# Revit family: Поли-Групп_КлапанОбратныйEAZ-RP_DN100-700
name_source: partatom
category: Арматура трубопроводов
units: mm (PartAtom-declared; Revit-internal decimal feet)

## family parameters
Всегда вертикально = Да
На основе рабочей плоскости = Нет
Общий = Нет
При загрузке вырезать с полостями = Нет
Размер круглого соединителя = Использовать диаметр
Тип детали = Нормальный

## types (19) — shared parameters
ADSK_URL страницы изделия = https://www.polycorr.ru
ADSK_Версия Revit = 2019
ADSK_Единица измерения = шт.
ADSK_Завод-изготовитель = ООО ПК Поли-Групп
ADSK_Количество = 1
ADSK_Материал = Высокопрочный чугун GGG-40
ADSK_Материал наименование = Высокопрочный чугун с шаровидным графитом (GGG-40)
Класс герметичности = А по ГОСТ Р 9544-2015
Материал диска = Высокотемпературная углеродистая сталь
Материал диска/шара/створки = Бронза CuSn10
Материал уплотнителя = NBR
Назначение = Для предотвращения обратного потока среды на горизонтальных трубопроводах
Покрытие = Высококачественное эпоксидное покрытие толщиной 300 мкм
Рабочая среда = Питьевая вода, техническая вода, канализационные стоки, морская вода
Разработчик = https://3dbim.pro
Срок службы = 50 лет
ТВ = КлапанОбратныйEAZ-RP_DN100-700_Поли-Групп
Температура рабочей среды = 0 до +70°С
Тип привода = Без привода
Тип присоединения = Фланцевое
zero-valued in all types: D1

## per-type parameters (varying)
| type | ADSK_Диаметр условный | ADSK_Марка | ADSK_Масса | ADSK_Масса_Текст | ADSK_Наименование | ADSK_Наименование краткое | D | D2 | DN | H1 | H2 | L | PN | b | d3 | d4 | d5 | f | r | Габаритные размеры |
| 200-10 | 200 мм | EAZ-DCh-2 DN200 PN10 | 117 | 117 | Клапан обратный EAZ RP с рычагом и противовесом для горизонтальной установки фланцевый DN200 PN10 | Клапан обратный EAZ RP DN200 PN10 | 340 мм | 266 мм | 200 мм | 40 мм | 250 мм | 500 мм | 10.0 бары | 20 мм | 240 мм | 220 мм | 200 мм | 3 мм | 156 мм | 295х340х460 |
| 250-10 | 250 мм | EAZ-DCh-2 DN250 PN10 | 170 | 170 | Клапан обратный EAZ RP с рычагом и противовесом для горизонтальной установки фланцевый DN250 PN10 | Клапан обратный EAZ RP DN250 PN10 | 405 мм | 319 мм | 250 мм | 49 мм | 284 мм | 600 мм | 10.0 бары | 22 мм | 300 мм | 275 мм | 250 мм | 3 мм | 195 мм | 355х405х536 |
| 300-10 | 300 мм | EAZ-DCh-2 DN300 PN10 | 263 | 263 | Клапан обратный EAZ RP с рычагом и противовесом для горизонтальной установки фланцевый DN300 PN10 | Клапан обратный EAZ RP DN300 PN10 | 445 мм | 370 мм | 300 мм | 58 мм | 318 мм | 700 мм | 10.0 бары | 25 мм | 360 мм | 330 мм | 300 мм | 4 мм | 234 мм | 400х445х599 |
| 350-10 | 350 мм | EAZ-DCh-2 DN350 PN10 | 320 | 320 | Клапан обратный EAZ RP с рычагом и противовесом для горизонтальной установки фланцевый DN350 PN10 | Клапан обратный EAZ RP DN350 PN10 | 520 мм | 429 мм | 350 мм | 69 мм | 354 мм | 800 мм | 10.0 бары | 25 мм | 420 мм | 385 мм | 350 мм | 4 мм | 273 мм | 470х520х683 |
| 400-10 | 400 мм | EAZ-DCh-2 DN400 PN10 | 485 | 485 | Клапан обратный EAZ RP с рычагом и противовесом для горизонтальной установки фланцевый DN400 PN10 | Клапан обратный EAZ RP DN400 PN10 | 656 мм | 480 мм | 400 мм | 79 мм | 390 мм | 900 мм | 10.0 бары | 25 мм | 480 мм | 440 мм | 400 мм | 4 мм | 312 мм | 515х656х797 |
| 500-10 | 500 мм | EAZ-DCh-2 DN500 PN10 | 620 | 620 | Клапан обратный EAZ RP с рычагом и противовесом для горизонтальной установки фланцевый DN500 PN10 | Клапан обратный EAZ RP DN500 PN10 | 670 мм | 582 мм | 500 мм | 62 мм | 497 мм | 1100 мм | 10.0 бары | 27 мм | 600 мм | 550 мм | 500 мм | 4 мм | 390 мм | 620х670х894 |
| 600-10 | 600 мм | EAZ-DCh-2 DN600 PN10 | 910 | 910 | Клапан обратный EAZ RP с рычагом и противовесом для горизонтальной установки фланцевый DN600 PN10 | Клапан обратный EAZ RP DN600 PN10 | 780 мм | 682 мм | 600 мм | 62 мм | 550 мм | 1300 мм | 10.0 бары | 30 мм | 720 мм | 660 мм | 600 мм | 5 мм | 468 мм | 725х780х1002 |
| 700-10 | 700 мм | EAZ-DCh-2 DN700 PN10 | 1380 | 1380 | Клапан обратный EAZ RP с рычагом и противовесом для горизонтальной установки фланцевый DN700 PN10 | Клапан обратный EAZ RP DN700 PN10 | 895 мм | 794 мм | 700 мм | 90 мм | 645 мм | 1500 мм | 10.0 бары | 33 мм | 840 мм | 770 мм | 700 мм | 5 мм | 546 мм | 840х895х1183 |
| 100-16 | 100 мм | EAZ-DCh-2 DN100 PN16 | 40 | 40 | Клапан обратный EAZ RP с рычагом и противовесом для горизонтальной установки фланцевый DN100 PN16 | Клапан обратный EAZ RP DN100 PN16 | 220 мм | 156 мм | 100 мм | 20 мм | 150 мм | 300 мм | 16.0 бары | 19 мм | 120 мм | 110 мм | 100 мм | 3 мм | 78 мм | 180х220х280 |
| 125-16 | 125 мм | EAZ-DCh-2 DN125 PN16 | 65 | 65 | Клапан обратный EAZ RP с рычагом и противовесом для горизонтальной установки фланцевый DN125 PN16 | Клапан обратный EAZ RP DN125 PN16 | 250 мм | 184 мм | 125 мм | 25 мм | 175 мм | 350 мм | 16.0 бары | 19 мм | 150 мм | 138 мм | 125 мм | 3 мм | 98 мм | 210х250х325 |
| 150-16 | 150 мм | EAZ-DCh-2 DN150 PN16 | 80 | 80 | Клапан обратный EAZ RP с рычагом и противовесом для горизонтальной установки фланцевый DN150 PN16 | Клапан обратный EAZ RP DN150 PN16 | 285 мм | 211 мм | 150 мм | 35 мм | 200 мм | 400 мм | 16.0 бары | 19 мм | 180 мм | 165 мм | 150 мм | 3 мм | 117 мм | 240х285х378 |
| 200-16 | 200 мм | EAZ-DCh-2 DN200 PN16 | 125 | 125 | Клапан обратный EAZ RP с рычагом и противовесом для горизонтальной установки фланцевый DN200 PN16 | Клапан обратный EAZ RP DN200 PN16 | 340 мм | 266 мм | 200 мм | 40 мм | 250 мм | 500 мм | 16.0 бары | 20 мм | 240 мм | 220 мм | 200 мм | 3 мм | 156 мм | 295х340х460 |
| 250-16 | 250 мм | EAZ-DCh-2 DN250 PN16 | 198 | 198 | Клапан обратный EAZ RP с рычагом и противовесом для горизонтальной установки фланцевый DN250 PN16 | Клапан обратный EAZ RP DN250 PN16 | 405 мм | 319 мм | 250 мм | 49 мм | 284 мм | 600 мм | 16.0 бары | 22 мм | 300 мм | 275 мм | 250 мм | 3 мм | 195 мм | 355х405х536 |
| 300-16 | 300 мм | EAZ-DCh-2 DN300 PN16 | 285 | 285 | Клапан обратный EAZ RP с рычагом и противовесом для горизонтальной установки фланцевый DN300 PN16 | Клапан обратный EAZ RP DN300 PN16 | 460 мм | 370 мм | 300 мм | 58 мм | 318 мм | 700 мм | 16.0 бары | 25 мм | 360 мм | 330 мм | 300 мм | 4 мм | 234 мм | 410х460х606 |
| 350-16 | 350 мм | EAZ-DCh-2 DN350 PN16 | 360 | 360 | Клапан обратный EAZ RP с рычагом и противовесом для горизонтальной установки фланцевый DN350 PN16 | Клапан обратный EAZ RP DN350 PN16 | 520 мм | 429 мм | 350 мм | 69 мм | 354 мм | 800 мм | 16.0 бары | 27 мм | 420 мм | 385 мм | 350 мм | 4 мм | 273 мм | 470х520х683 |
| 400-16 | 400 мм | EAZ-DCh-2 DN400 PN16 | 515 | 515 | Клапан обратный EAZ RP с рычагом и противовесом для горизонтальной установки фланцевый DN400 PN16 | Клапан обратный EAZ RP DN400 PN16 | 580 мм | 480 мм | 400 мм | 79 мм | 390 мм | 900 мм | 16.0 бары | 28 мм | 480 мм | 440 мм | 400 мм | 4 мм | 312 мм | 525х580х759 |
| 500-16 | 500 мм | EAZ-DCh-2 DN500 PN16 | 700 | 700 | Клапан обратный EAZ RP с рычагом и противовесом для горизонтальной установки фланцевый DN500 PN16 | Клапан обратный EAZ RP DN500 PN16 | 715 мм | 609 мм | 500 мм | 62 мм | 497 мм | 1100 мм | 16.0 бары | 32 мм | 600 мм | 550 мм | 500 мм | 4 мм | 390 мм | 650х715х917 |
| 600-16 | 600 мм | EAZ-DCh-2 DN600 PN16 | 985 | 985 | Клапан обратный EAZ RP с рычагом и противовесом для горизонтальной установки фланцевый DN600 PN16 | Клапан обратный EAZ RP DN600 PN16 | 840 мм | 720 мм | 600 мм | 62 мм | 550 мм | 1300 мм | 16.0 бары | 36 мм | 720 мм | 660 мм | 600 мм | 5 мм | 468 мм | 770х840х1032 |
| 700-16 | 700 мм | EAZ-DCh-2 DN700 PN16 | 1464 | 1464 | Клапан обратный EAZ RP с рычагом и противовесом для горизонтальной установки фланцевый DN700 PN16 | Клапан обратный EAZ RP DN700 PN16 | 910 мм | 794 мм | 700 мм | 90 мм | 645 мм | 1500 мм | 16.0 бары | 40 мм | 840 мм | 770 мм | 700 мм | 5 мм | 546 мм | 840х910х1190 |
